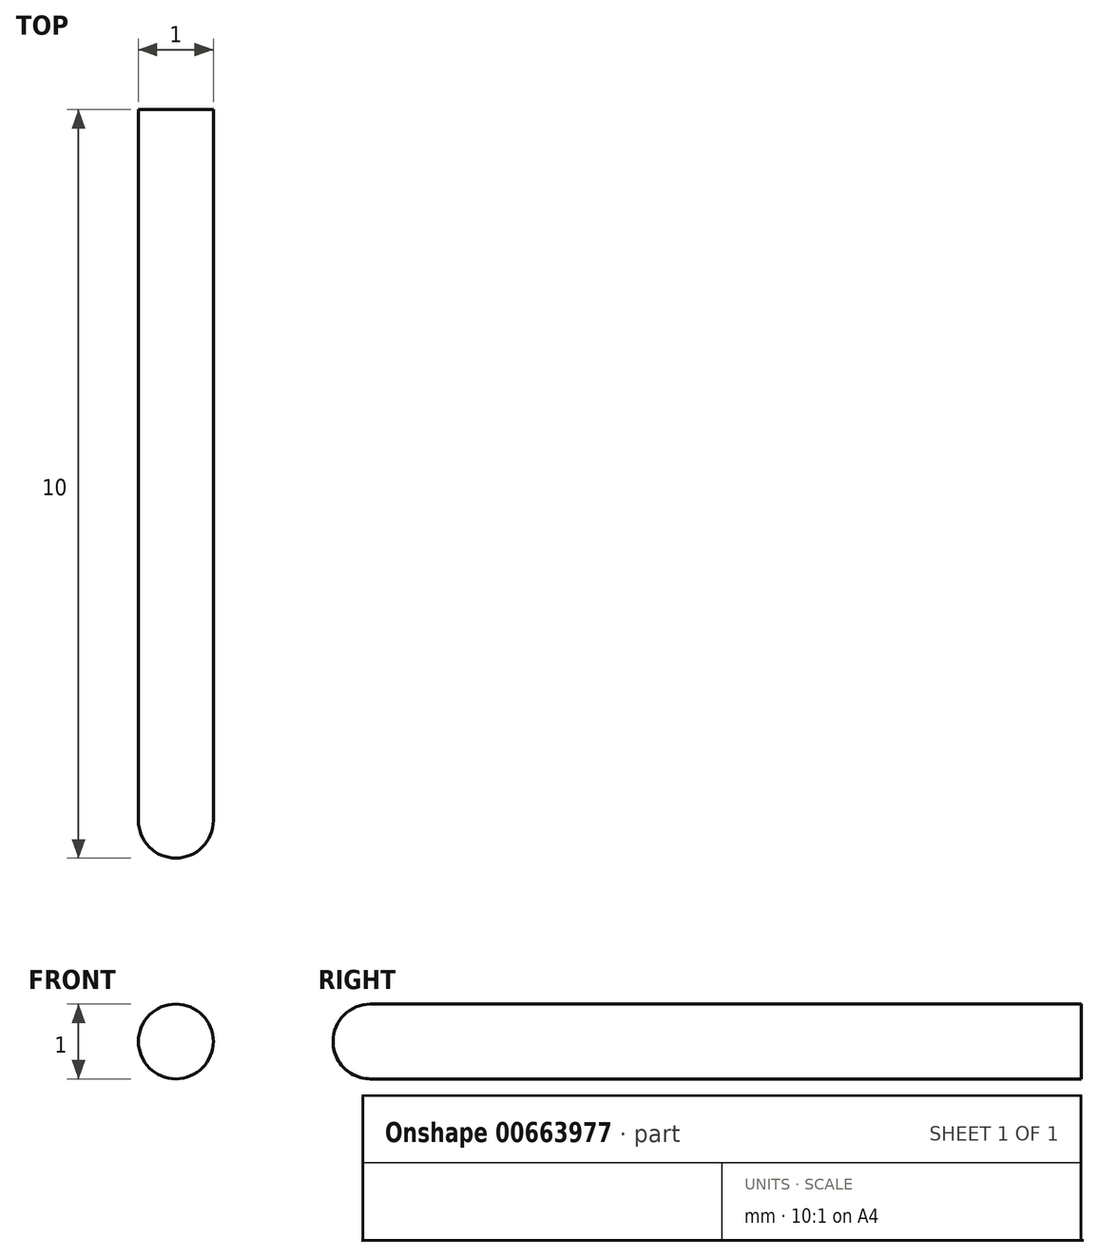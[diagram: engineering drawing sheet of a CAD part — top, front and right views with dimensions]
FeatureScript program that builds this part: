
annotation { "Feature Type Name" : "Feature", "Feature Type Description" : "" }
export const myFeature = defineFeature(function(context is Context, id is Id, definition is map)
    precondition{}
    {
        {
            var Q0;
            Q0=qCreatedBy(makeId("Front.planeOp"),FACE);
            var sketch = newSketch(context, id + "F0", { "sketchPlane" : qUnion([Q0])});
            skCircle(sketch, "E0", {"center": v(0, 0) * mm, "radius": 0.5 * mm});
            skSolve(sketch);
        }
        {
            var Q0;
            Q0 = qSketchRegion(id + "F0", true);
            extrude(context, id + "F1", {"entities" : qUnion([Q0]), "depth" : 10 * mm, "offsetDistance" : 25 * mm});
        }
        {
            var Q0;
            Q0=makeQuery(id+"F1.opExtrude","CAP_EDGE",EDGE,{"disambiguationData":[OSD([sQuery(id+"F0.wireOp",EDGE,"E0")])],"isStart":false});
            fillet(context, id + "F2", {"entities" : qUnion([Q0]), "radius" : .5 * mm, "tangentPropagation" : true, "allowEdgeOverflow" : false});
        }
    });
